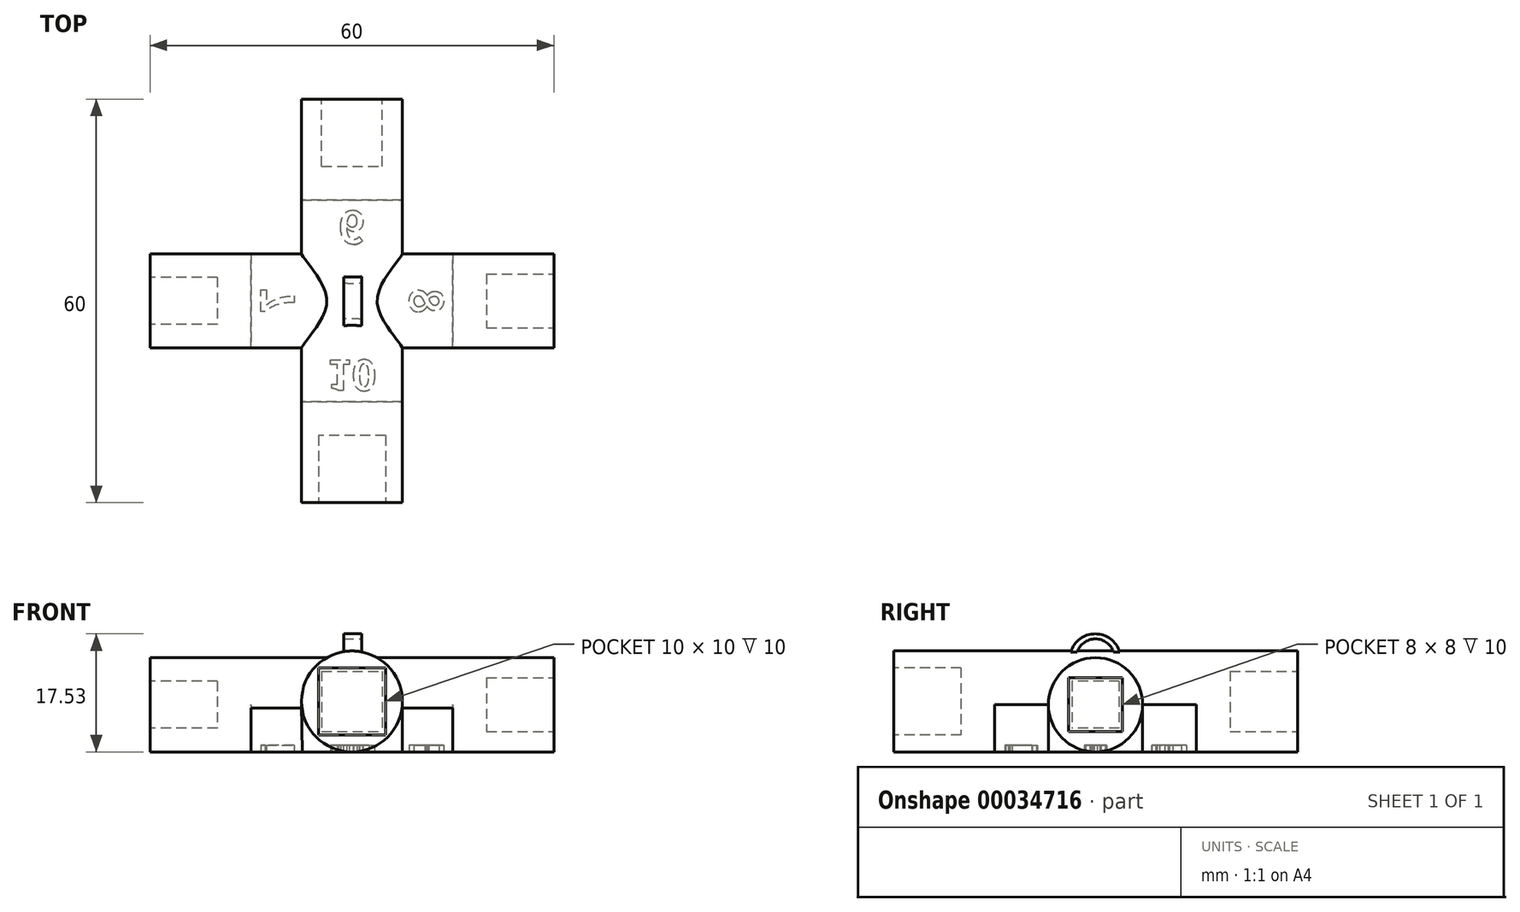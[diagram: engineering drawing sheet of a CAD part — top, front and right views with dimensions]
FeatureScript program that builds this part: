
annotation { "Feature Type Name" : "Feature", "Feature Type Description" : "" }
export const myFeature = defineFeature(function(context is Context, id is Id, definition is map)
    precondition{}
    {
        {
            var Q0;
            Q0=qCreatedBy(makeId("Right.planeOp"),FACE);
            var sketch = newSketch(context, id + "F0", { "sketchPlane" : qUnion([Q0])});
            skCircle(sketch, "E0", {"center": v(0, 0) * mm, "radius": 7 * mm});
            skArc(sketch, "E1", {"start": v(2.77, 6.43) * mm, "mid": v(-0.04, 9.79) * mm, "end": v(-2.82, 6.4) * mm});
            skArc(sketch, "E2", {"start": v(3.69, 5.95) * mm, "mid": v(-0.07, 10.53) * mm, "end": v(-3.77, 5.9) * mm});
            skLineSegment(sketch, "E3", {"start": v(7, 0) * mm, "end": v(7, -7) * mm});
            skLineSegment(sketch, "E4", {"start": v(7, -7) * mm, "end": v(-6.98, -7) * mm});
            skLineSegment(sketch, "E5", {"start": v(-6.98, -7) * mm, "end": v(-6.98, 0) * mm});
            skSolve(sketch);
        }
        {
            var Q0;
            {var subQ0=sQuery(id+"F0.wireOp",EDGE,"E1");var subQ1=sQuery(id+"F0.wireOp",EDGE,"E0");var subQ2=makeQuery(id+"F0.imprint","INTERSECT",VERTEX,{"disambiguationData":[OD(0.0)],"derivedFrom":[subQ1,subQ0]});Q0=makeQuery(id+"F0.imprint","IMPRINT",FACE,{"disambiguationData":[TD([[makeQuery(id+"F0.imprint","IMPRINT",EDGE,{"disambiguationData":[TD([[subQ2,1.0]])],"derivedFrom":subQ1}),1.0]])]});}
            extrude(context, id + "F1", {"entities" : qUnion([Q0]), "depth" : 60 * mm, "symmetric" : true});
        }
        {
            var Q0;
            Q0=makeQuery(id+"F1.opExtrude","CAP_FACE",FACE,{"disambiguationData":[OSD([sQuery(id+"F0.wireOp",EDGE,"E0")])],"isStart":true});
            var sketch = newSketch(context, id + "F2", { "sketchPlane" : qUnion([Q0])});
            skLineSegment(sketch, "E6.bottom", {"start": v(-3.5, 3.5) * mm, "end": v(3.5, 3.5) * mm});
            skLineSegment(sketch, "E6.top", {"start": v(-3.5, -3.5) * mm, "end": v(3.5, -3.5) * mm});
            skLineSegment(sketch, "E6.left", {"start": v(-3.5, 3.5) * mm, "end": v(-3.5, -3.5) * mm});
            skLineSegment(sketch, "E6.right", {"start": v(3.5, 3.5) * mm, "end": v(3.5, -3.5) * mm});
            skPoint(sketch, "E6.middle", {"position": v(0, 0) * mm});
            skSolve(sketch);
        }
        {
            var Q0;
            Q0=makeQuery(id+"F2.imprint","IMPRINT",FACE,{"disambiguationData":[TD([[makeQuery(id+"F2.imprint","IMPRINT",EDGE,{"derivedFrom":sQuery(id+"F2.wireOp",EDGE,"E6.bottom")}),-1.0]])]});
            extrude(context, id + "F3", {"entities" : qUnion([Q0]), "operationType" : NewBodyOperationType.REMOVE, "oppositeDirection" : true, "depth" : 10 * mm});
        }
        {
            var Q0;
            Q0=makeQuery(id+"F1.opExtrude","CAP_FACE",FACE,{"disambiguationData":[OSD([sQuery(id+"F0.wireOp",EDGE,"E0")])],"isStart":false});
            var sketch = newSketch(context, id + "F4", { "sketchPlane" : qUnion([Q0])});
            skLineSegment(sketch, "E7.bottom", {"start": v(4, 4) * mm, "end": v(-4, 4) * mm});
            skLineSegment(sketch, "E7.top", {"start": v(4, -4) * mm, "end": v(-4, -4) * mm});
            skLineSegment(sketch, "E7.left", {"start": v(4, 4) * mm, "end": v(4, -4) * mm});
            skLineSegment(sketch, "E7.right", {"start": v(-4, 4) * mm, "end": v(-4, -4) * mm});
            skPoint(sketch, "E7.middle", {"position": v(0, 0) * mm});
            skSolve(sketch);
        }
        {
            var Q0;
            Q0=makeQuery(id+"F4.imprint","IMPRINT",FACE,{"disambiguationData":[TD([[makeQuery(id+"F4.imprint","IMPRINT",EDGE,{"derivedFrom":sQuery(id+"F4.wireOp",EDGE,"E7.bottom")}),1.0]])]});
            extrude(context, id + "F5", {"entities" : qUnion([Q0]), "operationType" : NewBodyOperationType.REMOVE, "oppositeDirection" : true, "depth" : 10 * mm});
        }
        {
            var Q0;
            Q0=qCreatedBy(makeId("Front.planeOp"),FACE);
            var sketch = newSketch(context, id + "F6", { "sketchPlane" : qUnion([Q0])});
            skCircle(sketch, "E8", {"center": v(0, 0.5) * mm, "radius": 7.5 * mm});
            skLineSegment(sketch, "E9", {"start": v(7.48, 0) * mm, "end": v(7.48, -7) * mm});
            skLineSegment(sketch, "E10", {"start": v(7.48, -7) * mm, "end": v(-7.4, -7) * mm});
            skLineSegment(sketch, "E11", {"start": v(-7.48, 0) * mm, "end": v(-7.4, -7) * mm});
            skSolve(sketch);
        }
        {
            var Q0;
            Q0=makeQuery(id+"F6.imprint","IMPRINT",FACE,{"disambiguationData":[TD([[makeQuery(id+"F6.imprint","IMPRINT",EDGE,{"derivedFrom":sQuery(id+"F6.wireOp",EDGE,"E8")}),1.0]])]});
            extrude(context, id + "F7", {"entities" : qUnion([Q0]), "operationType" : NewBodyOperationType.ADD, "depth" : 60 * mm, "symmetric" : true});
        }
        {
            var Q0;
            {var subQ0=sQuery(id+"F0.wireOp",EDGE,"E1");Q0=makeQuery(id+"F0.imprint","IMPRINT",FACE,{"disambiguationData":[TD([[makeQuery(id+"F0.imprint","IMPRINT",EDGE,{"derivedFrom":subQ0}),-1.0]])]});}
            var Q1;
            Q1=makeQuery(id+"F1.opExtrude","CAP_FACE",FACE,{"disambiguationData":[OSD([sQuery(id+"F0.wireOp",EDGE,"E0")])],"isStart":false});
            extrude(context, id + "F8", {"entities" : qUnion([Q0]), "operationType" : NewBodyOperationType.ADD, "oppositeDirection" : true, "endBoundEntityFace" : qUnion([Q1]), "depth" : 1.25 * mm, "hasSecondDirection" : true, "secondDirectionOppositeDirection" : false, "secondDirectionDepth" : 1.46 * mm});
        }
        {
            var Q0;
            Q0=makeQuery(id+"F7.opExtrude","CAP_FACE",FACE,{"disambiguationData":[OSD([sQuery(id+"F6.wireOp",EDGE,"E8")])],"isStart":true});
            var sketch = newSketch(context, id + "F9", { "sketchPlane" : qUnion([Q0])});
            skLineSegment(sketch, "E12.bottom", {"start": v(4.5, 5) * mm, "end": v(-4.5, 5) * mm});
            skLineSegment(sketch, "E12.top", {"start": v(4.5, -4) * mm, "end": v(-4.5, -4) * mm});
            skLineSegment(sketch, "E12.left", {"start": v(4.5, 5) * mm, "end": v(4.5, -4) * mm});
            skLineSegment(sketch, "E12.right", {"start": v(-4.5, 5) * mm, "end": v(-4.5, -4) * mm});
            skSolve(sketch);
        }
        {
            var Q0;
            Q0=makeQuery(id+"F9.imprint","IMPRINT",FACE,{"disambiguationData":[TD([[makeQuery(id+"F9.imprint","IMPRINT",EDGE,{"derivedFrom":sQuery(id+"F9.wireOp",EDGE,"E12.bottom")}),1.0]])]});
            extrude(context, id + "F10", {"entities" : qUnion([Q0]), "operationType" : NewBodyOperationType.REMOVE, "oppositeDirection" : true, "depth" : 10 * mm});
        }
        {
            var Q0;
            Q0=makeQuery(id+"F7.opExtrude","CAP_FACE",FACE,{"disambiguationData":[OSD([sQuery(id+"F6.wireOp",EDGE,"E8")])],"isStart":false});
            var sketch = newSketch(context, id + "F11", { "sketchPlane" : qUnion([Q0])});
            skPoint(sketch, "E13.middle", {"position": v(0, 0) * mm});
            skLineSegment(sketch, "E14", {"start": v(0, 0) * mm, "end": v(0, 0.5) * mm});
            skPoint(sketch, "E15.middle", {"position": v(0, 0.5) * mm});
            skLineSegment(sketch, "E16.bottom", {"start": v(5, 5.5) * mm, "end": v(-5, 5.5) * mm});
            skLineSegment(sketch, "E16.top", {"start": v(5, -4.5) * mm, "end": v(-5, -4.5) * mm});
            skLineSegment(sketch, "E16.left", {"start": v(5, 5.5) * mm, "end": v(5, -4.5) * mm});
            skLineSegment(sketch, "E16.right", {"start": v(-5, 5.5) * mm, "end": v(-5, -4.5) * mm});
            skSolve(sketch);
        }
        {
            var Q0;
            Q0=makeQuery(id+"F11.imprint","IMPRINT",FACE,{"disambiguationData":[TD([[makeQuery(id+"F11.imprint","IMPRINT",EDGE,{"derivedFrom":sQuery(id+"F11.wireOp",EDGE,"E16.bottom")}),1.0]])]});
            extrude(context, id + "F12", {"entities" : qUnion([Q0]), "operationType" : NewBodyOperationType.REMOVE, "oppositeDirection" : true, "depth" : 10 * mm});
        }
        {
            var Q0;
            {var subQ0=sQuery(id+"F0.wireOp",EDGE,"E3");Q0=makeQuery(id+"F0.imprint","IMPRINT",FACE,{"disambiguationData":[TD([[makeQuery(id+"F0.imprint","IMPRINT",EDGE,{"derivedFrom":subQ0}),-1.0]])]});}
            var Q1;
            {var subQ0=sQuery(id+"F0.wireOp",EDGE,"E5");var subQ1=sQuery(id+"F0.wireOp",EDGE,"E0");var subQ2=makeQuery(id+"F0.imprint","INTERSECT",VERTEX,{"derivedFrom":[subQ1,subQ0]});Q1=makeQuery(id+"F0.imprint","IMPRINT",FACE,{"disambiguationData":[TD([[makeQuery(id+"F0.imprint","IMPRINT",EDGE,{"disambiguationData":[TD([[subQ2,-1.0]])],"derivedFrom":subQ1}),-1.0]])]});}
            extrude(context, id + "F13", {"entities" : qUnion([Q0, Q1]), "operationType" : NewBodyOperationType.ADD, "depth" : 30 * mm, "symmetric" : true});
        }
        {
            var Q0;
            {var subQ0=sQuery(id+"F6.wireOp",EDGE,"E9");Q0=makeQuery(id+"F6.imprint","IMPRINT",FACE,{"disambiguationData":[TD([[makeQuery(id+"F6.imprint","IMPRINT",EDGE,{"derivedFrom":subQ0}),-1.0]])]});}
            var Q1;
            {var subQ0=sQuery(id+"F6.wireOp",EDGE,"E11");Q1=makeQuery(id+"F6.imprint","IMPRINT",FACE,{"disambiguationData":[TD([[makeQuery(id+"F6.imprint","IMPRINT",EDGE,{"derivedFrom":subQ0}),1.0]])]});}
            extrude(context, id + "F14", {"entities" : qUnion([Q0, Q1]), "operationType" : NewBodyOperationType.ADD, "depth" : 30 * mm, "symmetric" : true});
        }
        {
            var Q0;
            {var subQ0=sQuery(id+"F0.wireOp",EDGE,"E4");Q0=makeQuery(id+"F13.boolean.opBoolean","MERGE",FACE,{"disambiguationData":[OD(0.0)],"derivedFrom":[makeQuery(id+"F13.opExtrude","SWEPT_FACE",FACE,{"disambiguationData":[OSD([subQ0]),TDD([makeQuery(id+"F0.imprint","IMPRINT",EDGE,{"disambiguationData":[TD([[makeQuery(id+"F0.imprint","INTERSECT",VERTEX,{"derivedFrom":[sQuery(id+"F0.wireOp",EDGE,"E3"),subQ0]}),-1.0]])],"derivedFrom":subQ0})])]}),makeQuery(id+"F13.opExtrude","SWEPT_FACE",FACE,{"disambiguationData":[OSD([subQ0]),TDD([makeQuery(id+"F0.imprint","IMPRINT",EDGE,{"disambiguationData":[TD([[makeQuery(id+"F0.imprint","INTERSECT",VERTEX,{"derivedFrom":[subQ0,sQuery(id+"F0.wireOp",EDGE,"E5")]}),1.0]])],"derivedFrom":subQ0})])]})]});}
            var sketch = newSketch(context, id + "F15", { "sketchPlane" : qUnion([Q0])});
            skText(sketch, "E17", { "text": "7", "fontName": "NotoSansCJKsc-Bold.otf"});
            skLineSegment(sketch, "E18.bottom", {"start": v(-15, -7) * mm, "end": v(-7, -7) * mm});
            skLineSegment(sketch, "E18.top", {"start": v(-15, 6.98) * mm, "end": v(-7, 6.98) * mm});
            skLineSegment(sketch, "E18.left", {"start": v(-15, -7) * mm, "end": v(-15, 6.98) * mm});
            skLineSegment(sketch, "E18.right", {"start": v(-7, -7) * mm, "end": v(-7, 6.98) * mm, "construction": true});
            skLineSegment(sketch, "E19", {"start": v(-15, 0) * mm, "end": v(-7, 0) * mm, "construction": true});
            skLineSegment(sketch, "E20", {"start": v(-13.4, 2) * mm, "end": v(-15, 2) * mm});
            skLineSegment(sketch, "E21", {"start": v(-8.6, 2) * mm, "end": v(-7, 2) * mm});
            skFitSpline(sketch, "E22.0.0", {"points": [v(0.15, -7) * mm, v(5.1, -7) * mm, v(10.05, -7) * mm, v(15, -7) * mm]});
            skFitSpline(sketch, "E22.0.1", {"points": [v(0.15, -7) * mm, v(5.1, -7) * mm, v(10.05, -7) * mm, v(15, -7) * mm]});
            skLineSegment(sketch, "E22.0.2", {"start": v(15, -7) * mm, "end": v(15, 0) * mm});
            skLineSegment(sketch, "E22.0.3", {"start": v(15, 0) * mm, "end": v(15, 6.98) * mm});
            skFitSpline(sketch, "E22.0.4", {"points": [v(15, 6.98) * mm, v(10.05, 6.98) * mm, v(5.1, 6.98) * mm, v(0.15, 6.98) * mm]});
            skFitSpline(sketch, "E22.0.5", {"points": [v(15, 6.98) * mm, v(10.05, 6.98) * mm, v(5.1, 6.98) * mm, v(0.15, 6.98) * mm]});
            skFitSpline(sketch, "E22.0.6", {"points": [v(0.15, 6.98) * mm, v(0.15, 2.32) * mm, v(0.15, -2.34) * mm, v(0.15, -7) * mm]});
            skLineSegment(sketch, "E23.0.0", {"start": v(7.48, -15) * mm, "end": v(7.48, -7) * mm});
            skFitSpline(sketch, "E23.0.1", {"points": [v(7.48, -7) * mm, v(5.04, -7) * mm, v(2.6, -7) * mm, v(0.15, -7) * mm]});
            skFitSpline(sketch, "E23.0.2", {"points": [v(0.15, -7) * mm, v(0.15, -2.34) * mm, v(0.15, 2.32) * mm, v(0.15, 6.98) * mm]});
            skFitSpline(sketch, "E23.0.3", {"points": [v(0.15, 6.98) * mm, v(2.6, 6.98) * mm, v(5.04, 6.98) * mm, v(7.48, 6.98) * mm]});
            skLineSegment(sketch, "E23.0.4", {"start": v(7.48, 6.98) * mm, "end": v(7.48, 15) * mm});
            skLineSegment(sketch, "E23.0.5", {"start": v(7.48, 15) * mm, "end": v(0, 15) * mm});
            skLineSegment(sketch, "E23.0.6", {"start": v(0, 15) * mm, "end": v(-7.4, 15) * mm});
            skFitSpline(sketch, "E23.0.7", {"points": [v(-7.4, 15) * mm, v(-7.4, 12.33) * mm, v(-7.4, 9.65) * mm, v(-7.4, 6.98) * mm]});
            skFitSpline(sketch, "E23.0.8", {"points": [v(-7.4, 6.98) * mm, v(-4.99, 6.98) * mm, v(-2.57, 6.98) * mm, v(-0.16, 6.98) * mm]});
            skFitSpline(sketch, "E23.0.9", {"points": [v(-0.16, 6.98) * mm, v(-0.16, 2.32) * mm, v(-0.16, -2.34) * mm, v(-0.16, -7) * mm]});
            skFitSpline(sketch, "E23.0.10", {"points": [v(-0.16, -7) * mm, v(-2.57, -7) * mm, v(-4.99, -7) * mm, v(-7.4, -7) * mm]});
            skFitSpline(sketch, "E23.0.11", {"points": [v(-7.4, -7) * mm, v(-7.4, -9.67) * mm, v(-7.4, -12.33) * mm, v(-7.4, -15) * mm]});
            skLineSegment(sketch, "E23.0.12", {"start": v(-7.4, -15) * mm, "end": v(0, -15) * mm});
            skLineSegment(sketch, "E23.0.13", {"start": v(0, -15) * mm, "end": v(7.48, -15) * mm});
            skFitSpline(sketch, "E24.0.1", {"points": [v(7.48, -7) * mm, v(5.04, -7) * mm, v(2.6, -7) * mm, v(0.15, -7) * mm]});
            skFitSpline(sketch, "E24.0.2", {"points": [v(0.15, -7) * mm, v(0.15, -2.34) * mm, v(0.15, 2.32) * mm, v(0.15, 6.98) * mm]});
            skFitSpline(sketch, "E24.0.3", {"points": [v(0.15, 6.98) * mm, v(2.6, 6.98) * mm, v(5.04, 6.98) * mm, v(7.48, 6.98) * mm]});
            skFitSpline(sketch, "E24.0.7", {"points": [v(-7.4, 15) * mm, v(-7.4, 12.33) * mm, v(-7.4, 9.65) * mm, v(-7.4, 6.98) * mm]});
            skFitSpline(sketch, "E24.0.8", {"points": [v(-7.4, 6.98) * mm, v(-4.99, 6.98) * mm, v(-2.57, 6.98) * mm, v(-0.16, 6.98) * mm]});
            skFitSpline(sketch, "E24.0.9", {"points": [v(-0.16, 6.98) * mm, v(-0.16, 2.32) * mm, v(-0.16, -2.34) * mm, v(-0.16, -7) * mm]});
            skFitSpline(sketch, "E24.0.10", {"points": [v(-0.16, -7) * mm, v(-2.57, -7) * mm, v(-4.99, -7) * mm, v(-7.4, -7) * mm]});
            skFitSpline(sketch, "E24.0.11", {"points": [v(-7.4, -7) * mm, v(-7.4, -9.67) * mm, v(-7.4, -12.33) * mm, v(-7.4, -15) * mm]});
            skLineSegment(sketch, "E25.bottom", {"start": v(15, 6.98) * mm, "end": v(7, 6.98) * mm});
            skLineSegment(sketch, "E25.top", {"start": v(15, -7) * mm, "end": v(7, -7) * mm});
            skLineSegment(sketch, "E25.left", {"start": v(15, 6.98) * mm, "end": v(15, -7) * mm});
            skLineSegment(sketch, "E25.right", {"start": v(7, 6.98) * mm, "end": v(7, -7) * mm, "construction": true});
            skLineSegment(sketch, "E26.bottom", {"start": v(-7.4, 10.43) * mm, "end": v(7.48, 10.43) * mm, "construction": true});
            skLineSegment(sketch, "E26.top", {"start": v(-7.4, 15) * mm, "end": v(7.48, 15) * mm});
            skLineSegment(sketch, "E26.left", {"start": v(-7.4, 10.43) * mm, "end": v(-7.4, 15) * mm});
            skLineSegment(sketch, "E26.right", {"start": v(7.48, 10.43) * mm, "end": v(7.48, 15) * mm});
            skLineSegment(sketch, "E27.bottom", {"start": v(-7.4, -15) * mm, "end": v(7.48, -15) * mm});
            skLineSegment(sketch, "E27.top", {"start": v(-7.4, -9.81) * mm, "end": v(7.48, -9.81) * mm, "construction": true});
            skLineSegment(sketch, "E27.left", {"start": v(-7.4, -15) * mm, "end": v(-7.4, -9.81) * mm});
            skLineSegment(sketch, "E27.right", {"start": v(7.48, -15) * mm, "end": v(7.48, -9.81) * mm});
            skText(sketch, "E28", { "text": "8", "fontName": "NotoSansCJKsc-Bold.otf"});
            skLineSegment(sketch, "E29", {"start": v(15, 0) * mm, "end": v(7, 0) * mm, "construction": true});
            skLineSegment(sketch, "E30", {"start": v(13.4, -2) * mm, "end": v(15, -2) * mm});
            skLineSegment(sketch, "E31", {"start": v(8.6, -2) * mm, "end": v(7, -2) * mm});
            skText(sketch, "E32", { "text": "10", "fontName": "NotoSansCJKsc-Bold.otf"});
            skPoint(sketch, "E32.firstSnap0", {"position": v(-3.7, 15) * mm});
            skLineSegment(sketch, "E33", {"start": v(-0.16, 6.98) * mm, "end": v(0.15, 6.98) * mm});
            skLineSegment(sketch, "E34", {"start": v(-0.16, -7) * mm, "end": v(0.15, -7) * mm});
            skLineSegment(sketch, "E35", {"start": v(0, 15) * mm, "end": v(0, 6.98) * mm, "construction": true});
            skLineSegment(sketch, "E36", {"start": v(3.7, 13.23) * mm, "end": v(3.7, 15) * mm, "construction": true});
            skLineSegment(sketch, "E37", {"start": v(3.7, 8.75) * mm, "end": v(3.7, 6.98) * mm, "construction": true});
            skText(sketch, "E38", { "text": "6", "fontName": "NotoSansCJKsc-Bold.otf"});
            skLineSegment(sketch, "E39", {"start": v(0, -15) * mm, "end": v(0, -7) * mm, "construction": true});
            skLineSegment(sketch, "E40", {"start": v(-2.01, -13.4) * mm, "end": v(-2.01, -15) * mm});
            skLineSegment(sketch, "E41", {"start": v(-2.01, -8.6) * mm, "end": v(-2.01, -7) * mm});
            const initialGuessF15  = {"E17": [-0.0086, -0.002, 0, 1, 0.00479], "E28": [0.0086, 0.002, 0, -1, 0.0048], "E32": [-0.0037, 0.00875, 1, 0, 0.00448], "E38": [-0.00201, -0.0134, 1, 0, 0.0048]};
            skSetInitialGuess(sketch, initialGuessF15);
            skSolve(sketch);
        }
        {
            var Q0;
            Q0=makeQuery(id+"F15.imprint","IMPRINT",FACE,{"disambiguationData":[TD([[makeQuery(id+"F15.imprint","IMPRINT",EDGE,{"derivedFrom":sQuery(id+"F15.wireOp",EDGE,"E17.sketch_text.stroke-0")}),1.0]])]});
            var Q1;
            Q1=makeQuery(id+"F15.imprint","IMPRINT",FACE,{"disambiguationData":[TD([[makeQuery(id+"F15.imprint","IMPRINT",EDGE,{"derivedFrom":sQuery(id+"F15.wireOp",EDGE,"E28.sketch_text.stroke-0")}),1.0]])]});
            var Q2;
            Q2=makeQuery(id+"F15.imprint","IMPRINT",FACE,{"disambiguationData":[TD([[makeQuery(id+"F15.imprint","IMPRINT",EDGE,{"derivedFrom":sQuery(id+"F15.wireOp",EDGE,"E32.sketch_text.stroke-11")}),1.0]])]});
            var Q3;
            Q3=makeQuery(id+"F15.imprint","IMPRINT",FACE,{"disambiguationData":[TD([[makeQuery(id+"F15.imprint","IMPRINT",EDGE,{"derivedFrom":sQuery(id+"F15.wireOp",EDGE,"E32.sketch_text.stroke-0")}),1.0]])]});
            var Q4;
            Q4=makeQuery(id+"F15.imprint","IMPRINT",FACE,{"disambiguationData":[TD([[makeQuery(id+"F15.imprint","IMPRINT",EDGE,{"derivedFrom":sQuery(id+"F15.wireOp",EDGE,"E38.sketch_text.stroke-0")}),1.0]])]});
            extrude(context, id + "F16", {"entities" : qUnion([Q0, Q1, Q2, Q3, Q4]), "operationType" : NewBodyOperationType.REMOVE, "oppositeDirection" : true, "depth" : 1 * mm});
        }
    });
